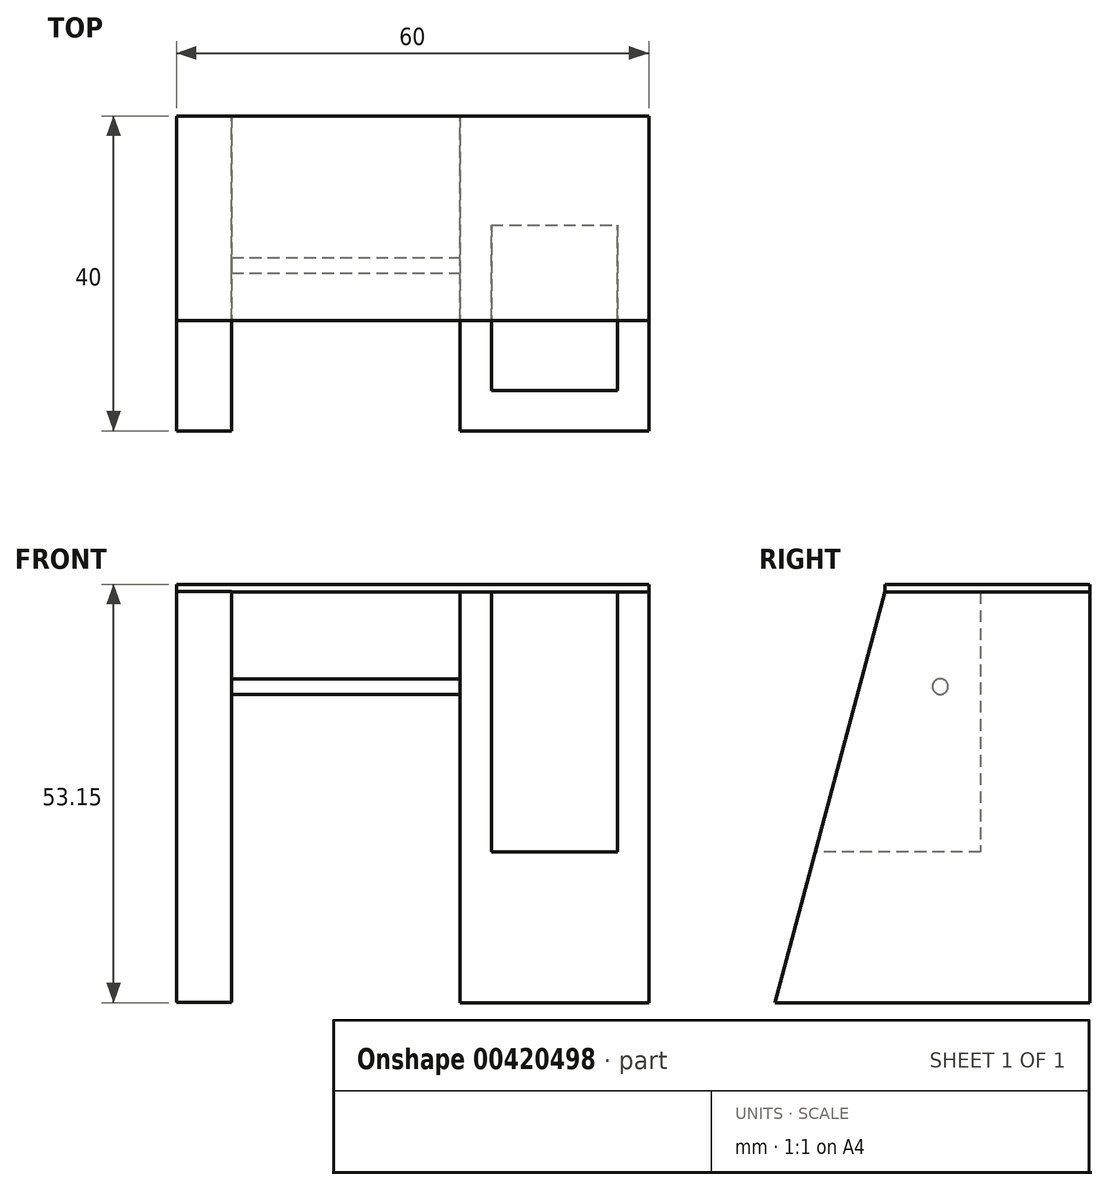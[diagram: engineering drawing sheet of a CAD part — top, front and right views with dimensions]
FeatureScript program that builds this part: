
annotation { "Feature Type Name" : "Feature", "Feature Type Description" : "" }
export const myFeature = defineFeature(function(context is Context, id is Id, definition is map)
    precondition{}
    {
        {
            var Q0;
            Q0=qCreatedBy(makeId("Right.planeOp"),FACE);
            var sketch = newSketch(context, id + "F0", { "sketchPlane" : qUnion([Q0])});
            skLineSegment(sketch, "E0", {"start": v(12.56, 29.42) * mm, "end": v(12.56, -22.73) * mm});
            skLineSegment(sketch, "E1", {"start": v(12.56, -22.73) * mm, "end": v(-27.44, -22.73) * mm});
            skLineSegment(sketch, "E2", {"start": v(-27.44, -22.73) * mm, "end": v(-13.43, 29.42) * mm});
            skLineSegment(sketch, "E3", {"start": v(-13.43, 29.42) * mm, "end": v(12.56, 29.42) * mm});
            skSolve(sketch);
        }
        {
            var Q0;
            Q0 = qSketchRegion(id + "F0", true);
            extrude(context, id + "F1", {"entities" : qUnion([Q0]), "depth" : 24 * mm});
        }
        {
            var Q0;
            Q0=qCreatedBy(makeId("Right.planeOp"),FACE);
            cPlane(context, id + "F2", {"entities" : qUnion([Q0]), "cplaneType" : CPlaneType.OFFSET, "offset" : 12 * mm, "width" : 150 * mm, "height" : 150 * mm});
        }
        {
            var Q0;
            Q0=qCreatedBy(id+"F2.planeOp",FACE);
            var sketch = newSketch(context, id + "F3", { "sketchPlane" : qUnion([Q0])});
            skLineSegment(sketch, "E4.0", {"start": v(-13.43, 29.42) * mm, "end": v(12.56, 29.42) * mm});
            skLineSegment(sketch, "E5.0", {"start": v(-27.44, -22.73) * mm, "end": v(-13.43, 29.42) * mm});
            skLineSegment(sketch, "E6", {"start": v(-1.3, 29.42) * mm, "end": v(-1.3, -3.58) * mm});
            skLineSegment(sketch, "E7", {"start": v(-1.3, -3.58) * mm, "end": v(-22.3, -3.58) * mm});
            skSolve(sketch);
        }
        {
            var Q0;
            {var subQ3=sQuery(id+"F3.wireOp",EDGE,"E6");Q0=makeQuery(id+"F3.imprint","IMPRINT",FACE,{"disambiguationData":[TD([[makeQuery(id+"F3.imprint","IMPRINT",EDGE,{"derivedFrom":subQ3}),-1.0]])]});}
            extrude(context, id + "F4", {"entities" : qUnion([Q0]), "operationType" : NewBodyOperationType.REMOVE, "endBound" : BoundingType.SYMMETRIC, "oppositeDirection" : true, "depth" : 16 * mm});
        }
        {
            var Q0;
            Q0=qCreatedBy(makeId("Right.planeOp"),FACE);
            cPlane(context, id + "F5", {"entities" : qUnion([Q0]), "cplaneType" : CPlaneType.OFFSET, "offset" : 29 * mm, "oppositeDirection" : true, "width" : 150 * mm, "height" : 150 * mm});
        }
        {
            var Q0;
            Q0=qCreatedBy(id+"F5.planeOp",FACE);
            var sketch = newSketch(context, id + "F6", { "sketchPlane" : qUnion([Q0])});
            skLineSegment(sketch, "E8", {"start": v(12.56, 29.48) * mm, "end": v(12.56, -22.67) * mm});
            skLineSegment(sketch, "E9", {"start": v(12.56, -22.67) * mm, "end": v(-27.44, -22.67) * mm});
            skLineSegment(sketch, "E10", {"start": v(-27.44, -22.67) * mm, "end": v(-13.43, 29.48) * mm});
            skLineSegment(sketch, "E11", {"start": v(-13.43, 29.48) * mm, "end": v(12.56, 29.48) * mm});
            skLineSegment(sketch, "E12.0", {"start": v(-27.44, -22.73) * mm, "end": v(-13.43, 29.42) * mm});
            skSolve(sketch);
        }
        {
            var Q0;
            Q0=makeQuery(id+"F6.imprint","IMPRINT",FACE,{"disambiguationData":[TD([[makeQuery(id+"F6.imprint","IMPRINT",EDGE,{"derivedFrom":sQuery(id+"F6.wireOp",EDGE,"E8")}),-1.0]])]});
            extrude(context, id + "F7", {"entities" : qUnion([Q0]), "oppositeDirection" : true, "depth" : 7 * mm});
        }
        {
            var Q0;
            Q0=makeQuery(id+"F1.opExtrude","CAP_FACE",FACE,{"disambiguationData":[OSD([sQuery(id+"F0.wireOp",EDGE,"E0"),sQuery(id+"F0.wireOp",EDGE,"E1"),sQuery(id+"F0.wireOp",EDGE,"E2"),sQuery(id+"F0.wireOp",EDGE,"E3")])],"isStart":true});
            var sketch = newSketch(context, id + "F8", { "sketchPlane" : qUnion([Q0])});
            skCircle(sketch, "E13", {"center": v(6.43, 17.42) * mm, "radius": 1 * mm});
            skSolve(sketch);
        }
        {
            var Q0;
            Q0=makeQuery(id+"F8.imprint","IMPRINT",FACE,{"disambiguationData":[TD([[makeQuery(id+"F8.imprint","IMPRINT",EDGE,{"derivedFrom":sQuery(id+"F8.wireOp",EDGE,"E13")}),1.0]])]});
            extrude(context, id + "F9", {"entities" : qUnion([Q0]), "endBound" : BoundingType.UP_TO_NEXT, "depth" : 25 * mm});
        }
        {
            var Q0;
            Q0=makeQuery(id+"F1.opExtrude","SWEPT_FACE",FACE,{"disambiguationData":[OSD([sQuery(id+"F0.wireOp",EDGE,"E3")])]});
            cPlane(context, id + "F10", {"entities" : qUnion([Q0]), "cplaneType" : CPlaneType.OFFSET, "offset" : 0 * mm, "width" : 150 * mm, "height" : 150 * mm});
        }
        {
            var Q0;
            Q0=qCreatedBy(id+"F10.planeOp",FACE);
            var sketch = newSketch(context, id + "F11", { "sketchPlane" : qUnion([Q0])});
            skLineSegment(sketch, "E14.bottom", {"start": v(-36, 12.56) * mm, "end": v(24, 12.56) * mm});
            skLineSegment(sketch, "E14.top", {"start": v(-36, -13.43) * mm, "end": v(24, -13.43) * mm});
            skLineSegment(sketch, "E14.left", {"start": v(-36, 12.56) * mm, "end": v(-36, -13.43) * mm});
            skLineSegment(sketch, "E14.right", {"start": v(24, 12.56) * mm, "end": v(24, -13.43) * mm});
            skLineSegment(sketch, "E15.0", {"start": v(24, 12.56) * mm, "end": v(0, 12.56) * mm});
            skLineSegment(sketch, "E16.0", {"start": v(24, -13.43) * mm, "end": v(24, 12.56) * mm});
            skLineSegment(sketch, "E17.0", {"start": v(-36, -13.43) * mm, "end": v(-36, 12.56) * mm});
            skLineSegment(sketch, "E18.0", {"start": v(24, -13.43) * mm, "end": v(20, -13.43) * mm});
            skSolve(sketch);
        }
        {
            var Q0;
            {var subQ1=sQuery(id+"F11.wireOp",EDGE,"E14.bottom");Q0=makeQuery(id+"F11.imprint","IMPRINT",FACE,{"disambiguationData":[TD([[makeQuery(id+"F11.imprint","IMPRINT",EDGE,{"derivedFrom":subQ1}),-1.0]])]});}
            extrude(context, id + "F12", {"entities" : qUnion([Q0]), "depth" : 1 * mm});
        }
    });
